AUTODESK INVENTOR PART (.ipt)
format: ipt  version: 2015 (Build 190159000, 159)  size: 544,256 bytes
history: native  units: mm
features: other x19, loft x3, pattern_circular x3, sketch x1
ambient origin geometry x6: Origin, XZ Plane, X Axis, Y Axis, Z Axis, Center Point
bodies: Solid1 (feature_tree), 实体草图 (feature_tree)
feature tree (26):
  other  "网格平面 2"
  other  "齿实体"
  other  "齿平面"
  other  "起始草图"
  loft  "Loft"
  pattern_circular  "Circular Pattern"  [2 undecoded]
  other  "三维草图 (右)"
  other  "终止平面 (右)"
  loft  "放样 (右)"
  pattern_circular  "环形阵列 (右)"  [2 undecoded]
  other  "三维草图 (左)"
  other  "终止平面 (左)"
  loft  "放样 (左)"
  pattern_circular  "环形阵列 (左)"  [2 undecoded]
  other  "固定实体"
  other  "网格平面"
  other  "上平面"
  other  "齿实体草图"
  other  "终止平面"
  other  "终止草图"
  other  "Helical Curve Left"
  other  "终止草图 (左)"
  sketch  "Sketch6"  dims[d0=60.0mm d1=53.16948mm d2=65.6921mm d3=37.9mm d4=89.051317mm d5=90.0deg d7=11.826909mm d8=13.097268mm d9=26.531224mm d11=38.23mm d12=7.072733mm d15=7.832434mm d16=15.866214mm d17=0.0mm d18=90.0deg d19=0.0mm d20=90.0deg d21=200.0mm d22=360.0deg d26=393.171382mm d27=36.268162mm d28=60.0mm d29=-3.217506mm d30=7.072733mm d31=7.832434mm d32=15.866214mm d35=0.0mm d37=0.0mm d39=0.0mm d40=90.0deg d41=200.0mm d42=360.0deg d46=90.0deg d47=90.0deg d48=0.0mm d49=0.0mm d50=90.0deg d51=1.570796mm d52=0.0mm d53=0.0mm d54=0.0mm d56=18.716423mm d57=36.602777mm d58=27.230777mm d59=21.889208mm d60=16.28456mm d61=21.889208mm d62=16.28456mm d65=393.171382mm d66=31.5mm d67=60.0mm d68=-3.217506mm d69=36.268162mm d70=7.832434mm d71=15.866214mm d72=7.072733mm d73=16.28456mm d74=21.889208mm d75=0.0mm d77=0.0mm d79=0.0mm d80=90.0deg d81=200.0mm d82=360.0deg d84=10.0mm d85=20.0mm d86=20.0mm d87=10.0mm d88=0.0mm d89=0.0mm d90=90.0deg d91=90.0deg d92=90.0deg d93=90.0deg]
  other  "Srf1"
  other  "Helical Curve Right"
  other  "终止草图 (右)"
note: 6 required parameter values undecoded (feature->parameter linkage not recoverable at this tier; creation-order binding heuristic only, values carry confidence <= 0.55)
